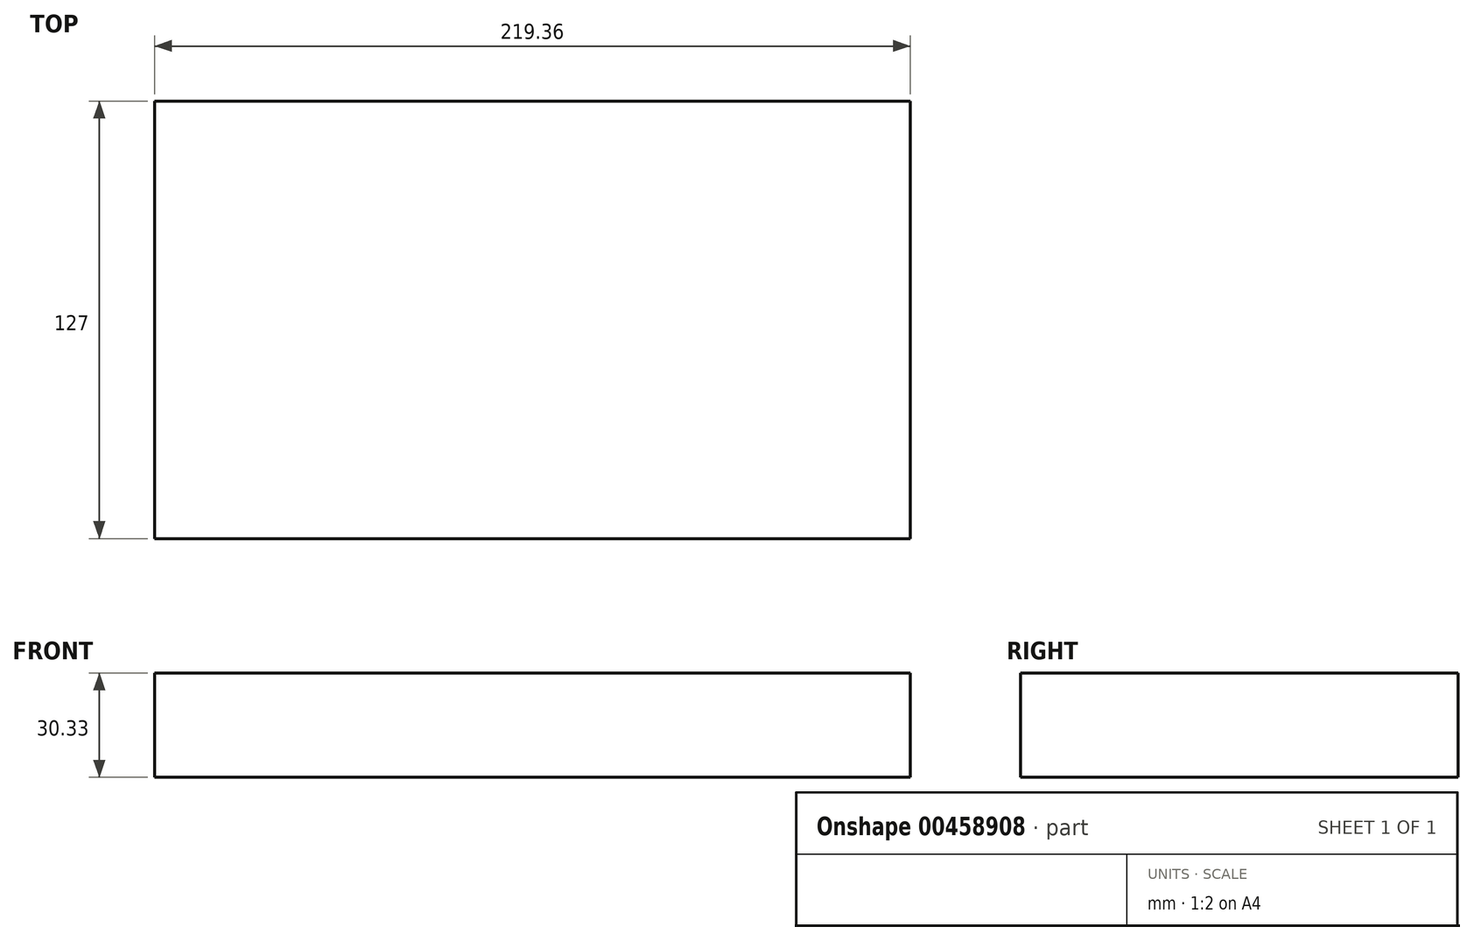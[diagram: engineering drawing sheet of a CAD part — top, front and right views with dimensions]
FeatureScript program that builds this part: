
annotation { "Feature Type Name" : "Feature", "Feature Type Description" : "" }
export const myFeature = defineFeature(function(context is Context, id is Id, definition is map)
    precondition{}
    {
        {
            var Q0;
            Q0=qCreatedBy(makeId("Front.planeOp"),FACE);
            var sketch = newSketch(context, id + "F0", { "sketchPlane" : qUnion([Q0])});
            skLineSegment(sketch, "E0.bottom", {"start": v(-75.9, 30.33) * mm, "end": v(16.46, 30.33) * mm});
            skLineSegment(sketch, "E0.top", {"start": v(-75.9, 0) * mm, "end": v(16.46, 0) * mm});
            skLineSegment(sketch, "E0.left", {"start": v(-75.9, 30.33) * mm, "end": v(-75.9, 0) * mm});
            skLineSegment(sketch, "E0.right", {"start": v(16.46, 30.33) * mm, "end": v(16.46, 0) * mm});
            skSolve(sketch);
        }
        {
            var Q0;
            Q0=makeQuery(id+"F0.imprint","IMPRINT",FACE,{"disambiguationData":[TD([[makeQuery(id+"F0.imprint","IMPRINT",EDGE,{"derivedFrom":sQuery(id+"F0.wireOp",EDGE,"E0.bottom")}),-1.0]])]});
            extrude(context, id + "F1", {"entities" : qUnion([Q0]), "depth" : 127 * mm});
        }
        {
            var Q0;
            Q0=makeQuery(id+"F1.opExtrude","SWEPT_FACE",FACE,{"disambiguationData":[OSD([sQuery(id+"F0.wireOp",EDGE,"E0.right")])]});
            var sketch = newSketch(context, id + "F2", { "sketchPlane" : qUnion([Q0])});
            skLineSegment(sketch, "E1", {"start": v(-127, 30.33) * mm, "end": v(-99.93, 81.94) * mm});
            skLineSegment(sketch, "E2", {"start": v(0, 30.33) * mm, "end": v(-25.9, 81.94) * mm});
            skLineSegment(sketch, "E3", {"start": v(-99.93, 81.94) * mm, "end": v(-25.9, 81.94) * mm});
            skSolve(sketch);
        }
        {
            var Q0;
            Q0=makeQuery(id+"F1.opExtrude","SWEPT_FACE",FACE,{"disambiguationData":[OSD([sQuery(id+"F0.wireOp",EDGE,"E0.left")])]});
            extrude(context, id + "F3", {"entities" : qUnion([Q0]), "operationType" : NewBodyOperationType.ADD, "depth" : 127 * mm});
        }
    });
